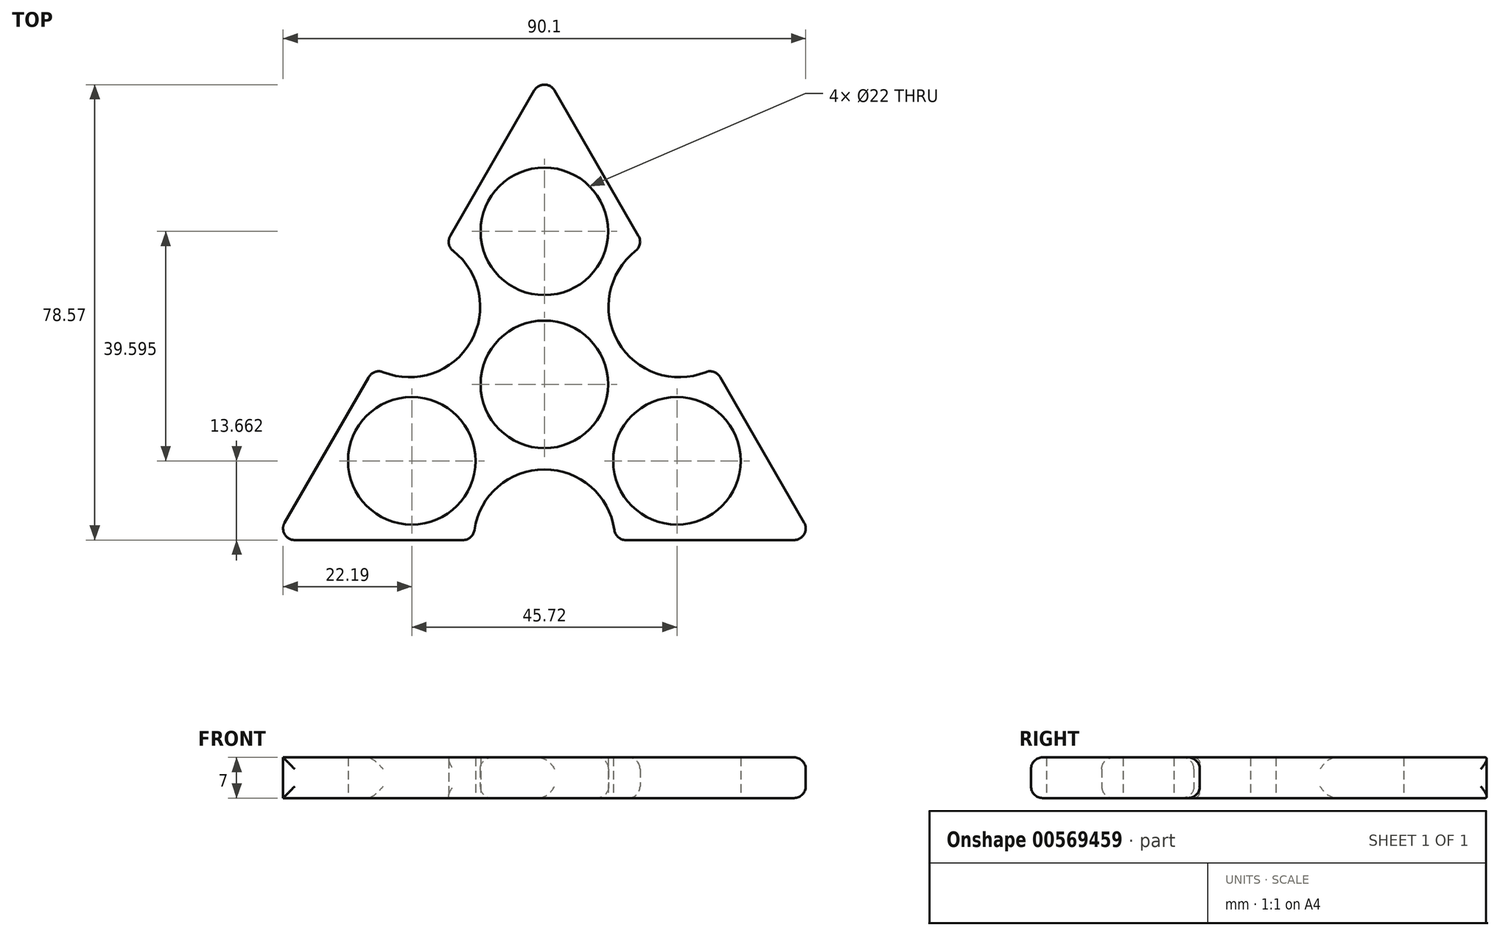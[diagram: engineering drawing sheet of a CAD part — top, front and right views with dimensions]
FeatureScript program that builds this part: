
annotation { "Feature Type Name" : "Feature", "Feature Type Description" : "" }
export const myFeature = defineFeature(function(context is Context, id is Id, definition is map)
    precondition{}
    {
        {
            var Q0;
            Q0=qCreatedBy(makeId("Top.planeOp"),FACE);
            var sketch = newSketch(context, id + "F0", { "sketchPlane" : qUnion([Q0])});
            skCircle(sketch, "E0", {"center": v(0, 0) * mm, "radius": 11 * mm});
            skCircle(sketch, "E1", {"center": v(0, 0) * mm, "radius": 26.4 * mm});
            skLineSegment(sketch, "E2", {"start": v(0, 0) * mm, "end": v(22.86, -13.2) * mm});
            skLineSegment(sketch, "E3", {"start": v(0, 0) * mm, "end": v(-22.86, -13.2) * mm});
            skLineSegment(sketch, "E4", {"start": v(0, 0) * mm, "end": v(0, 26.4) * mm});
            skLineSegment(sketch, "E5", {"start": v(0, 26.4) * mm, "end": v(-22.86, -13.2) * mm});
            skLineSegment(sketch, "E6", {"start": v(22.86, -13.2) * mm, "end": v(-22.86, -13.2) * mm});
            skLineSegment(sketch, "E7", {"start": v(0, 26.4) * mm, "end": v(22.86, -13.2) * mm});
            skCircle(sketch, "E8", {"center": v(-22.86, -13.2) * mm, "radius": 11 * mm});
            skCircle(sketch, "E9", {"center": v(22.86, -13.2) * mm, "radius": 11 * mm});
            skCircle(sketch, "E10", {"center": v(0, 26.4) * mm, "radius": 11 * mm});
            skCircle(sketch, "E11", {"center": v(0, 0) * mm, "radius": 53.71 * mm});
            skCircle(sketch, "E12", {"center": v(0, 26.4) * mm, "radius": 13.5 * mm});
            skCircle(sketch, "E13", {"center": v(22.86, -13.2) * mm, "radius": 13.5 * mm});
            skCircle(sketch, "E14", {"center": v(-22.86, -13.2) * mm, "radius": 13.5 * mm});
            skLineSegment(sketch, "E15", {"start": v(0, 0) * mm, "end": v(-46.52, -26.86) * mm});
            skLineSegment(sketch, "E16", {"start": v(-46.52, -26.86) * mm, "end": v(0, 0) * mm});
            skLineSegment(sketch, "E17", {"start": v(0, 0) * mm, "end": v(46.52, -26.86) * mm});
            skLineSegment(sketch, "E18", {"start": v(0, 0) * mm, "end": v(0, 53.71) * mm});
            skLineSegment(sketch, "E19", {"start": v(0, 53.71) * mm, "end": v(-46.52, -26.86) * mm});
            skLineSegment(sketch, "E20", {"start": v(-46.52, -26.86) * mm, "end": v(46.52, -26.86) * mm});
            skLineSegment(sketch, "E21", {"start": v(46.52, -26.86) * mm, "end": v(0, 53.71) * mm});
            skArc(sketch, "E22", {"start": v(-17.16, 23.99) * mm, "mid": v(-12.7, 7.33) * mm, "end": v(-29.35, 2.87) * mm});
            skArc(sketch, "E23", {"start": v(12.2, -26.86) * mm, "mid": v(0, -14.66) * mm, "end": v(-12.2, -26.86) * mm});
            skArc(sketch, "E24", {"start": v(17.16, 23.99) * mm, "mid": v(12.7, 7.33) * mm, "end": v(29.35, 2.87) * mm});
            skSolve(sketch);
        }
        {
            var Q0;
            {var subQ0=sQuery(id+"F0.wireOp",EDGE,"E12");var subQ1=sQuery(id+"F0.wireOp",EDGE,"E1");var subQ2=makeQuery(id+"F0.imprint","INTERSECT",VERTEX,{"disambiguationData":[OD(1.0)],"derivedFrom":[subQ1,subQ0]});Q0=makeQuery(id+"F0.imprint","IMPRINT",FACE,{"disambiguationData":[TD([[makeQuery(id+"F0.imprint","IMPRINT",EDGE,{"disambiguationData":[TD([[subQ2,-1.0]])],"derivedFrom":subQ1}),1.0]])]});}
            var Q1;
            {var subQ1=sQuery(id+"F0.wireOp",EDGE,"E1");var subQ7=sQuery(id+"F0.wireOp",EDGE,"E14");var subQ9=makeQuery(id+"F0.imprint","INTERSECT",VERTEX,{"disambiguationData":[OD(1.0)],"derivedFrom":[subQ1,subQ7]});Q1=makeQuery(id+"F0.imprint","IMPRINT",FACE,{"disambiguationData":[TD([[makeQuery(id+"F0.imprint","IMPRINT",EDGE,{"disambiguationData":[TD([[subQ9,-1.0]])],"derivedFrom":subQ1}),1.0]])]});}
            var Q2;
            {var subQ3=sQuery(id+"F0.wireOp",EDGE,"E16");var subQ5=sQuery(id+"F0.wireOp",EDGE,"E0");var subQ6=makeQuery(id+"F0.imprint","INTERSECT",VERTEX,{"derivedFrom":[subQ5,subQ3]});Q2=makeQuery(id+"F0.imprint","IMPRINT",FACE,{"disambiguationData":[TD([[makeQuery(id+"F0.imprint","IMPRINT",EDGE,{"disambiguationData":[TD([[subQ6,-1.0]])],"derivedFrom":subQ5}),-1.0]])]});}
            var Q3;
            {var subQ3=sQuery(id+"F0.wireOp",EDGE,"E18");var subQ9=sQuery(id+"F0.wireOp",EDGE,"E0");var subQ10=makeQuery(id+"F0.imprint","INTERSECT",VERTEX,{"derivedFrom":[subQ9,subQ3]});Q3=makeQuery(id+"F0.imprint","IMPRINT",FACE,{"disambiguationData":[TD([[makeQuery(id+"F0.imprint","IMPRINT",EDGE,{"disambiguationData":[TD([[subQ10,1.0]])],"derivedFrom":subQ9}),-1.0]])]});}
            var Q4;
            {var subQ5=sQuery(id+"F0.wireOp",EDGE,"E24");var subQ6=sQuery(id+"F0.wireOp",EDGE,"E1");var subQ10=makeQuery(id+"F0.imprint","INTERSECT",VERTEX,{"disambiguationData":[OD(0.0)],"derivedFrom":[subQ6,subQ5]});Q4=makeQuery(id+"F0.imprint","IMPRINT",FACE,{"disambiguationData":[TD([[makeQuery(id+"F0.imprint","IMPRINT",EDGE,{"disambiguationData":[TD([[subQ10,-1.0]])],"derivedFrom":subQ6}),1.0]])]});}
            var Q5;
            {var subQ0=sQuery(id+"F0.wireOp",EDGE,"E9");var subQ1=sQuery(id+"F0.wireOp",EDGE,"E1");var subQ2=makeQuery(id+"F0.imprint","INTERSECT",VERTEX,{"disambiguationData":[OD(1.0)],"derivedFrom":[subQ1,subQ0]});Q5=makeQuery(id+"F0.imprint","IMPRINT",FACE,{"disambiguationData":[TD([[makeQuery(id+"F0.imprint","IMPRINT",EDGE,{"disambiguationData":[TD([[subQ2,-1.0]])],"derivedFrom":subQ1}),1.0]])]});}
            var Q6;
            {var subQ0=sQuery(id+"F0.wireOp",EDGE,"E13");var subQ1=sQuery(id+"F0.wireOp",EDGE,"E1");var subQ2=makeQuery(id+"F0.imprint","INTERSECT",VERTEX,{"disambiguationData":[OD(0.0)],"derivedFrom":[subQ1,subQ0]});Q6=makeQuery(id+"F0.imprint","IMPRINT",FACE,{"disambiguationData":[TD([[makeQuery(id+"F0.imprint","IMPRINT",EDGE,{"disambiguationData":[TD([[subQ2,-1.0]])],"derivedFrom":subQ1}),-1.0]])]});}
            var Q7;
            {var subQ0=sQuery(id+"F0.wireOp",EDGE,"E9");var subQ1=sQuery(id+"F0.wireOp",EDGE,"E1");var subQ2=makeQuery(id+"F0.imprint","INTERSECT",VERTEX,{"disambiguationData":[OD(1.0)],"derivedFrom":[subQ1,subQ0]});Q7=makeQuery(id+"F0.imprint","IMPRINT",FACE,{"disambiguationData":[TD([[makeQuery(id+"F0.imprint","IMPRINT",EDGE,{"disambiguationData":[TD([[subQ2,-1.0]])],"derivedFrom":subQ1}),-1.0]])]});}
            var Q8;
            {var subQ0=sQuery(id+"F0.wireOp",EDGE,"E13");var subQ1=sQuery(id+"F0.wireOp",EDGE,"E1");var subQ2=makeQuery(id+"F0.imprint","INTERSECT",VERTEX,{"disambiguationData":[OD(0.0)],"derivedFrom":[subQ1,subQ0]});Q8=makeQuery(id+"F0.imprint","IMPRINT",FACE,{"disambiguationData":[TD([[makeQuery(id+"F0.imprint","IMPRINT",EDGE,{"disambiguationData":[TD([[subQ2,-1.0]])],"derivedFrom":subQ1}),1.0]])]});}
            var Q9;
            {var subQ0=sQuery(id+"F0.wireOp",EDGE,"E8");var subQ1=sQuery(id+"F0.wireOp",EDGE,"E1");var subQ2=makeQuery(id+"F0.imprint","INTERSECT",VERTEX,{"disambiguationData":[OD(1.0)],"derivedFrom":[subQ1,subQ0]});Q9=makeQuery(id+"F0.imprint","IMPRINT",FACE,{"disambiguationData":[TD([[makeQuery(id+"F0.imprint","IMPRINT",EDGE,{"disambiguationData":[TD([[subQ2,-1.0]])],"derivedFrom":subQ1}),-1.0]])]});}
            var Q10;
            {var subQ0=sQuery(id+"F0.wireOp",EDGE,"E14");var subQ1=sQuery(id+"F0.wireOp",EDGE,"E1");var subQ2=makeQuery(id+"F0.imprint","INTERSECT",VERTEX,{"disambiguationData":[OD(0.0)],"derivedFrom":[subQ1,subQ0]});Q10=makeQuery(id+"F0.imprint","IMPRINT",FACE,{"disambiguationData":[TD([[makeQuery(id+"F0.imprint","IMPRINT",EDGE,{"disambiguationData":[TD([[subQ2,-1.0]])],"derivedFrom":subQ1}),-1.0]])]});}
            var Q11;
            {var subQ0=sQuery(id+"F0.wireOp",EDGE,"E14");var subQ1=sQuery(id+"F0.wireOp",EDGE,"E1");var subQ2=makeQuery(id+"F0.imprint","INTERSECT",VERTEX,{"disambiguationData":[OD(0.0)],"derivedFrom":[subQ1,subQ0]});Q11=makeQuery(id+"F0.imprint","IMPRINT",FACE,{"disambiguationData":[TD([[makeQuery(id+"F0.imprint","IMPRINT",EDGE,{"disambiguationData":[TD([[subQ2,-1.0]])],"derivedFrom":subQ1}),1.0]])]});}
            var Q12;
            {var subQ0=sQuery(id+"F0.wireOp",EDGE,"E8");var subQ1=sQuery(id+"F0.wireOp",EDGE,"E1");var subQ2=makeQuery(id+"F0.imprint","INTERSECT",VERTEX,{"disambiguationData":[OD(1.0)],"derivedFrom":[subQ1,subQ0]});Q12=makeQuery(id+"F0.imprint","IMPRINT",FACE,{"disambiguationData":[TD([[makeQuery(id+"F0.imprint","IMPRINT",EDGE,{"disambiguationData":[TD([[subQ2,-1.0]])],"derivedFrom":subQ1}),1.0]])]});}
            var Q13;
            {var subQ0=sQuery(id+"F0.wireOp",EDGE,"E14");var subQ1=sQuery(id+"F0.wireOp",EDGE,"E6");var subQ2=makeQuery(id+"F0.imprint","INTERSECT",VERTEX,{"derivedFrom":[subQ1,subQ0]});Q13=makeQuery(id+"F0.imprint","IMPRINT",FACE,{"disambiguationData":[TD([[makeQuery(id+"F0.imprint","IMPRINT",EDGE,{"disambiguationData":[TD([[subQ2,-1.0]])],"derivedFrom":subQ1}),-1.0]])]});}
            var Q14;
            {var subQ0=sQuery(id+"F0.wireOp",EDGE,"E14");var subQ1=sQuery(id+"F0.wireOp",EDGE,"E5");var subQ2=makeQuery(id+"F0.imprint","INTERSECT",VERTEX,{"derivedFrom":[subQ1,subQ0]});Q14=makeQuery(id+"F0.imprint","IMPRINT",FACE,{"disambiguationData":[TD([[makeQuery(id+"F0.imprint","IMPRINT",EDGE,{"disambiguationData":[TD([[subQ2,-1.0]])],"derivedFrom":subQ1}),1.0]])]});}
            var Q15;
            {var subQ3=sQuery(id+"F0.wireOp",EDGE,"E16");var subQ9=sQuery(id+"F0.wireOp",EDGE,"E0");var subQ10=makeQuery(id+"F0.imprint","INTERSECT",VERTEX,{"derivedFrom":[subQ9,subQ3]});Q15=makeQuery(id+"F0.imprint","IMPRINT",FACE,{"disambiguationData":[TD([[makeQuery(id+"F0.imprint","IMPRINT",EDGE,{"disambiguationData":[TD([[subQ10,1.0]])],"derivedFrom":subQ9}),-1.0]])]});}
            var Q16;
            {var subQ0=sQuery(id+"F0.wireOp",EDGE,"E13");var subQ1=sQuery(id+"F0.wireOp",EDGE,"E7");var subQ2=makeQuery(id+"F0.imprint","INTERSECT",VERTEX,{"derivedFrom":[subQ1,subQ0]});Q16=makeQuery(id+"F0.imprint","IMPRINT",FACE,{"disambiguationData":[TD([[makeQuery(id+"F0.imprint","IMPRINT",EDGE,{"disambiguationData":[TD([[subQ2,-1.0]])],"derivedFrom":subQ1}),-1.0]])]});}
            var Q17;
            {var subQ0=sQuery(id+"F0.wireOp",EDGE,"E9");var subQ1=sQuery(id+"F0.wireOp",EDGE,"E6");var subQ2=makeQuery(id+"F0.imprint","INTERSECT",VERTEX,{"derivedFrom":[subQ1,subQ0]});Q17=makeQuery(id+"F0.imprint","IMPRINT",FACE,{"disambiguationData":[TD([[makeQuery(id+"F0.imprint","IMPRINT",EDGE,{"disambiguationData":[TD([[subQ2,-1.0]])],"derivedFrom":subQ1}),-1.0]])]});}
            var Q18;
            {var subQ0=sQuery(id+"F0.wireOp",EDGE,"E10");var subQ1=sQuery(id+"F0.wireOp",EDGE,"E1");var subQ2=makeQuery(id+"F0.imprint","INTERSECT",VERTEX,{"disambiguationData":[OD(1.0)],"derivedFrom":[subQ1,subQ0]});Q18=makeQuery(id+"F0.imprint","IMPRINT",FACE,{"disambiguationData":[TD([[makeQuery(id+"F0.imprint","IMPRINT",EDGE,{"disambiguationData":[TD([[subQ2,-1.0]])],"derivedFrom":subQ1}),1.0]])]});}
            var Q19;
            {var subQ0=sQuery(id+"F0.wireOp",EDGE,"E10");var subQ1=sQuery(id+"F0.wireOp",EDGE,"E5");var subQ2=makeQuery(id+"F0.imprint","INTERSECT",VERTEX,{"derivedFrom":[subQ1,subQ0]});Q19=makeQuery(id+"F0.imprint","IMPRINT",FACE,{"disambiguationData":[TD([[makeQuery(id+"F0.imprint","IMPRINT",EDGE,{"disambiguationData":[TD([[subQ2,-1.0]])],"derivedFrom":subQ1}),1.0]])]});}
            var Q20;
            {var subQ0=sQuery(id+"F0.wireOp",EDGE,"E10");var subQ1=sQuery(id+"F0.wireOp",EDGE,"E7");var subQ2=makeQuery(id+"F0.imprint","INTERSECT",VERTEX,{"derivedFrom":[subQ1,subQ0]});Q20=makeQuery(id+"F0.imprint","IMPRINT",FACE,{"disambiguationData":[TD([[makeQuery(id+"F0.imprint","IMPRINT",EDGE,{"disambiguationData":[TD([[subQ2,-1.0]])],"derivedFrom":subQ1}),-1.0]])]});}
            var Q21;
            {var subQ0=sQuery(id+"F0.wireOp",EDGE,"E12");var subQ1=sQuery(id+"F0.wireOp",EDGE,"E1");var subQ2=makeQuery(id+"F0.imprint","INTERSECT",VERTEX,{"disambiguationData":[OD(0.0)],"derivedFrom":[subQ1,subQ0]});Q21=makeQuery(id+"F0.imprint","IMPRINT",FACE,{"disambiguationData":[TD([[makeQuery(id+"F0.imprint","IMPRINT",EDGE,{"disambiguationData":[TD([[subQ2,-1.0]])],"derivedFrom":subQ1}),1.0]])]});}
            var Q22;
            {var subQ0=sQuery(id+"F0.wireOp",EDGE,"E12");var subQ1=sQuery(id+"F0.wireOp",EDGE,"E1");var subQ2=makeQuery(id+"F0.imprint","INTERSECT",VERTEX,{"disambiguationData":[OD(0.0)],"derivedFrom":[subQ1,subQ0]});Q22=makeQuery(id+"F0.imprint","IMPRINT",FACE,{"disambiguationData":[TD([[makeQuery(id+"F0.imprint","IMPRINT",EDGE,{"disambiguationData":[TD([[subQ2,-1.0]])],"derivedFrom":subQ1}),-1.0]])]});}
            var Q23;
            {var subQ0=sQuery(id+"F0.wireOp",EDGE,"E10");var subQ1=sQuery(id+"F0.wireOp",EDGE,"E1");var subQ2=makeQuery(id+"F0.imprint","INTERSECT",VERTEX,{"disambiguationData":[OD(1.0)],"derivedFrom":[subQ1,subQ0]});Q23=makeQuery(id+"F0.imprint","IMPRINT",FACE,{"disambiguationData":[TD([[makeQuery(id+"F0.imprint","IMPRINT",EDGE,{"disambiguationData":[TD([[subQ2,-1.0]])],"derivedFrom":subQ1}),-1.0]])]});}
            var Q24;
            {var subQ3=sQuery(id+"F0.wireOp",EDGE,"E24");var subQ7=sQuery(id+"F0.wireOp",EDGE,"E1");var subQ9=makeQuery(id+"F0.imprint","INTERSECT",VERTEX,{"disambiguationData":[OD(0.0)],"derivedFrom":[subQ7,subQ3]});Q24=makeQuery(id+"F0.imprint","IMPRINT",FACE,{"disambiguationData":[TD([[makeQuery(id+"F0.imprint","IMPRINT",EDGE,{"disambiguationData":[TD([[subQ9,-1.0]])],"derivedFrom":subQ7}),-1.0]])]});}
            var Q25;
            {var subQ3=sQuery(id+"F0.wireOp",EDGE,"E23");var subQ7=sQuery(id+"F0.wireOp",EDGE,"E1");var subQ9=makeQuery(id+"F0.imprint","INTERSECT",VERTEX,{"disambiguationData":[OD(1.0)],"derivedFrom":[subQ7,subQ3]});Q25=makeQuery(id+"F0.imprint","IMPRINT",FACE,{"disambiguationData":[TD([[makeQuery(id+"F0.imprint","IMPRINT",EDGE,{"disambiguationData":[TD([[subQ9,-1.0]])],"derivedFrom":subQ7}),-1.0]])]});}
            var Q26;
            {var subQ5=sQuery(id+"F0.wireOp",EDGE,"E1");var subQ7=sQuery(id+"F0.wireOp",EDGE,"E22");var subQ9=makeQuery(id+"F0.imprint","INTERSECT",VERTEX,{"disambiguationData":[OD(1.0)],"derivedFrom":[subQ5,subQ7]});Q26=makeQuery(id+"F0.imprint","IMPRINT",FACE,{"disambiguationData":[TD([[makeQuery(id+"F0.imprint","IMPRINT",EDGE,{"disambiguationData":[TD([[subQ9,-1.0]])],"derivedFrom":subQ5}),-1.0]])]});}
            var Q27;
            {var subQ5=sQuery(id+"F0.wireOp",EDGE,"E1");var subQ7=sQuery(id+"F0.wireOp",EDGE,"E14");var subQ9=makeQuery(id+"F0.imprint","INTERSECT",VERTEX,{"disambiguationData":[OD(1.0)],"derivedFrom":[subQ5,subQ7]});Q27=makeQuery(id+"F0.imprint","IMPRINT",FACE,{"disambiguationData":[TD([[makeQuery(id+"F0.imprint","IMPRINT",EDGE,{"disambiguationData":[TD([[subQ9,-1.0]])],"derivedFrom":subQ5}),-1.0]])]});}
            var Q28;
            {var subQ3=sQuery(id+"F0.wireOp",EDGE,"E12");var subQ5=sQuery(id+"F0.wireOp",EDGE,"E1");var subQ6=makeQuery(id+"F0.imprint","INTERSECT",VERTEX,{"disambiguationData":[OD(1.0)],"derivedFrom":[subQ5,subQ3]});Q28=makeQuery(id+"F0.imprint","IMPRINT",FACE,{"disambiguationData":[TD([[makeQuery(id+"F0.imprint","IMPRINT",EDGE,{"disambiguationData":[TD([[subQ6,-1.0]])],"derivedFrom":subQ5}),-1.0]])]});}
            var Q29;
            {var subQ3=sQuery(id+"F0.wireOp",EDGE,"E24");var subQ5=sQuery(id+"F0.wireOp",EDGE,"E1");var subQ6=makeQuery(id+"F0.imprint","INTERSECT",VERTEX,{"disambiguationData":[OD(1.0)],"derivedFrom":[subQ5,subQ3]});Q29=makeQuery(id+"F0.imprint","IMPRINT",FACE,{"disambiguationData":[TD([[makeQuery(id+"F0.imprint","IMPRINT",EDGE,{"disambiguationData":[TD([[subQ6,1.0]])],"derivedFrom":subQ5}),-1.0]])]});}
            extrude(context, id + "F1", {"entities" : qUnion([Q0, Q1, Q2, Q3, Q4, Q5, Q6, Q7, Q8, Q9, Q10, Q11, Q12, Q13, Q14, Q15, Q16, Q17, Q18, Q19, Q20, Q21, Q22, Q23, Q24, Q25, Q26, Q27, Q28, Q29]), "depth" : 7 * mm, "offsetDistance" : 25.4 * mm});
        }
        {
            var Q0;
            {var subQ0=sQuery(id+"F0.wireOp",EDGE,"E21");Q0=makeQuery(id+"F1.opExtrude","SWEPT_FACE",FACE,{"disambiguationData":[OSD([subQ0]),TDD([makeQuery(id+"F0.imprint","IMPRINT",EDGE,{"disambiguationData":[TD([[makeQuery(id+"F0.imprint","INTERSECT",VERTEX,{"disambiguationData":[OD(0.0)],"derivedFrom":[subQ0,sQuery(id+"F0.wireOp",EDGE,"E24")]}),-1.0]])],"derivedFrom":subQ0})])]});}
            var Q1;
            Q1=makeQuery(id+"F1.opExtrude","SWEPT_FACE",FACE,{"disambiguationData":[OSD([sQuery(id+"F0.wireOp",EDGE,"E24")])]});
            var Q2;
            {var subQ0=sQuery(id+"F0.wireOp",EDGE,"E21");Q2=makeQuery(id+"F1.opExtrude","SWEPT_FACE",FACE,{"disambiguationData":[OSD([subQ0]),TDD([makeQuery(id+"F0.imprint","IMPRINT",EDGE,{"disambiguationData":[TD([[makeQuery(id+"F0.imprint","INTERSECT",VERTEX,{"disambiguationData":[OD(1.0)],"derivedFrom":[subQ0,sQuery(id+"F0.wireOp",EDGE,"E24")]}),1.0]])],"derivedFrom":subQ0})])]});}
            var Q3;
            {var subQ0=sQuery(id+"F0.wireOp",EDGE,"E19");Q3=makeQuery(id+"F1.opExtrude","SWEPT_FACE",FACE,{"disambiguationData":[OSD([subQ0]),TDD([makeQuery(id+"F0.imprint","IMPRINT",EDGE,{"disambiguationData":[TD([[makeQuery(id+"F0.imprint","INTERSECT",VERTEX,{"disambiguationData":[OD(0.0)],"derivedFrom":[subQ0,sQuery(id+"F0.wireOp",EDGE,"E22")]}),1.0]])],"derivedFrom":subQ0})])]});}
            var Q4;
            Q4=makeQuery(id+"F1.opExtrude","SWEPT_FACE",FACE,{"disambiguationData":[OSD([sQuery(id+"F0.wireOp",EDGE,"E22")])]});
            var Q5;
            {var subQ0=sQuery(id+"F0.wireOp",EDGE,"E19");Q5=makeQuery(id+"F1.opExtrude","SWEPT_FACE",FACE,{"disambiguationData":[OSD([subQ0]),TDD([makeQuery(id+"F0.imprint","IMPRINT",EDGE,{"disambiguationData":[TD([[makeQuery(id+"F0.imprint","INTERSECT",VERTEX,{"disambiguationData":[OD(1.0)],"derivedFrom":[subQ0,sQuery(id+"F0.wireOp",EDGE,"E22")]}),-1.0]])],"derivedFrom":subQ0})])]});}
            var Q6;
            {var subQ0=sQuery(id+"F0.wireOp",EDGE,"E20");Q6=makeQuery(id+"F1.opExtrude","SWEPT_FACE",FACE,{"disambiguationData":[OSD([subQ0]),TDD([makeQuery(id+"F0.imprint","IMPRINT",EDGE,{"disambiguationData":[TD([[makeQuery(id+"F0.imprint","INTERSECT",VERTEX,{"disambiguationData":[OD(1.0)],"derivedFrom":[subQ0,sQuery(id+"F0.wireOp",EDGE,"E23")]}),1.0]])],"derivedFrom":subQ0})])]});}
            var Q7;
            Q7=makeQuery(id+"F1.opExtrude","SWEPT_FACE",FACE,{"disambiguationData":[OSD([sQuery(id+"F0.wireOp",EDGE,"E23")])]});
            var Q8;
            {var subQ0=sQuery(id+"F0.wireOp",EDGE,"E20");Q8=makeQuery(id+"F1.opExtrude","SWEPT_FACE",FACE,{"disambiguationData":[OSD([subQ0]),TDD([makeQuery(id+"F0.imprint","IMPRINT",EDGE,{"disambiguationData":[TD([[makeQuery(id+"F0.imprint","INTERSECT",VERTEX,{"disambiguationData":[OD(0.0)],"derivedFrom":[subQ0,sQuery(id+"F0.wireOp",EDGE,"E23")]}),-1.0]])],"derivedFrom":subQ0})])]});}
            fillet(context, id + "F2", {"entities" : qUnion([Q0, Q1, Q2, Q3, Q4, Q5, Q6, Q7, Q8]), "radius" : 2 * mm, "tangentPropagation" : true, "allowEdgeOverflow" : false});
        }
    });
